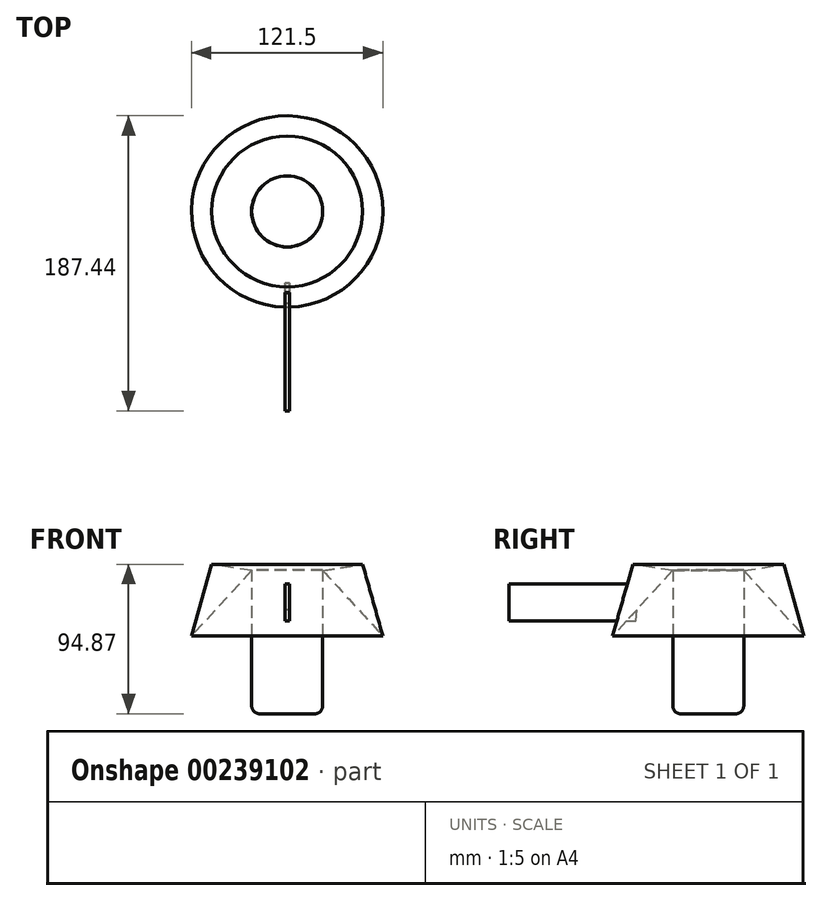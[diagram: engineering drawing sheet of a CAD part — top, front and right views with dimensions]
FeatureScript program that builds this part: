
annotation { "Feature Type Name" : "Feature", "Feature Type Description" : "" }
export const myFeature = defineFeature(function(context is Context, id is Id, definition is map)
    precondition{}
    {
        {
            assignVariable(context, id + "F0", {"name" : "v", "anyValue" : 3});
        }
        {
            var Q0;
            Q0=qCreatedBy(makeId("Front.planeOp"),FACE);
            var sketch = newSketch(context, id + "F1", { "sketchPlane" : qUnion([Q0])});
            skLineSegment(sketch, "E0", {"start": v(-47.93, 49.15) * mm, "end": v(-60.75, 3.66) * mm});
            skLineSegment(sketch, "E1", {"start": v(-60.75, 3.66) * mm, "end": v(-22.59, 45.18) * mm});
            skLineSegment(sketch, "E2", {"start": v(-22.59, 45.18) * mm, "end": v(-47.93, 49.15) * mm});
            skLineSegment(sketch, "E3", {"start": v(0, 57.08) * mm, "end": v(0, 0) * mm, "construction": true});
            skSolve(sketch);
        }
        {
            var Q0;
            Q0 = qSketchRegion(id + "F1", true);
            var Q1;
            Q1=sQuery(id+"F1.wireOp",EDGE,"E3");
            revolve(context, id + "F2", {"entities" : qUnion([Q0]), "axis" : qUnion([Q1]), "revolveType" : RevolveType.FULL});
        }
        {
            var Q0;
            Q0=qCreatedBy(makeId("Top.planeOp"),FACE);
            var sketch = newSketch(context, id + "F3", { "sketchPlane" : qUnion([Q0])});
            skCircle(sketch, "E4", {"center": v(0, 0) * mm, "radius": 22.52 * mm});
            skSolve(sketch);
        }
        {
            var Q0;
            Q0 = qSketchRegion(id + "F3", true);
            extrude(context, id + "F4", {"entities" : qUnion([Q0]), "endBound" : BoundingType.SYMMETRIC, "depth" : 91.44 * mm});
        }
        {
            var Q0;
            Q0=makeQuery(id+"F4.opExtrude","CAP_EDGE",EDGE,{"disambiguationData":[OSD([sQuery(id+"F3.wireOp",EDGE,"E4")])],"isStart":true});
            fillet(context, id + "F5", {"entities" : qUnion([Q0]), "radius" : 4.9 * mm, "tangentPropagation" : true, "allowEdgeOverflow" : false});
        }
        {
            var Q0;
            Q0=qCreatedBy(makeId("Right.planeOp"),FACE);
            var sketch = newSketch(context, id + "F6", { "sketchPlane" : qUnion([Q0])});
            skLineSegment(sketch, "E5", {"start": v(-44.57, 36.63) * mm, "end": v(-126.69, 36.63) * mm});
            skLineSegment(sketch, "E6", {"start": v(-126.69, 36.63) * mm, "end": v(-126.69, 13.13) * mm});
            skLineSegment(sketch, "E7", {"start": v(-126.69, 13.13) * mm, "end": v(-45.8, 13.13) * mm});
            skLineSegment(sketch, "E8", {"start": v(-45.8, 13.13) * mm, "end": v(-44.57, 36.63) * mm});
            skSolve(sketch);
        }
        {
            var Q0;
            Q0 = qSketchRegion(id + "F6", true);
            extrude(context, id + "F7", {"entities" : qUnion([Q0]), "operationType" : NewBodyOperationType.ADD, "endBound" : BoundingType.SYMMETRIC, "depth" : (getVariable(context, 'v')) * mm});
        }
    });
